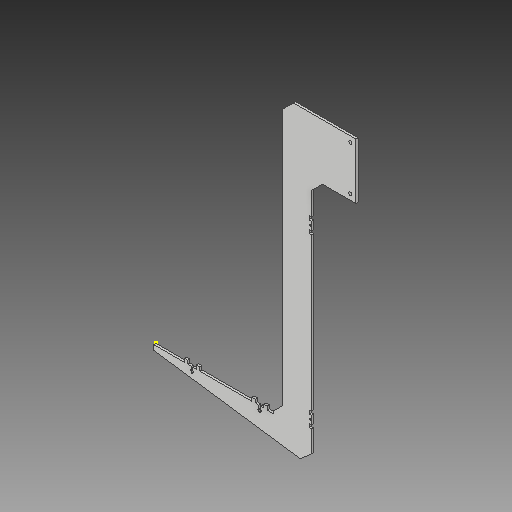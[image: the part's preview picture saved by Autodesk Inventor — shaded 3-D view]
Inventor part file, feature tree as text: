
AUTODESK INVENTOR PART (.ipt)
format: ipt  version: 2019 (Build 230136000, 136)  size: 232,960 bytes
history: native  units: in
note: dims shown in document units (in); Inventor stores cm internally (conversion verified against a paired STEP export)
features: reference x13, sketch x10, extrude x7, other x6, chamfer x2, helix x1
ambient origin geometry x8: Origin, YZ Plane, XZ Plane, XY Plane, X Axis, Y Axis, Z Axis, Center Point
bodies: Solid1 (feature_tree)
feature tree (39):
  extrude  "Extrusion1"  Depth=0.1575in
  chamfer  "Chamfer1"  Distance=0.1575in
  chamfer  "Chamfer2"  Distance=0.7874in Angle=45.0deg
  sketch  "Sketch2"  dims[d7=0.7874in d8=0.125in d9=45.0deg d10=3.1496in]
  sketch  "Sketch3"  dims[d11=3.937in d12=1.0in d13=0.0in]
  sketch  "Sketch4"  dims[d14=0.1181in d15=0.1181in]
  extrude  "Extrusion2"  Depth=3.1496in
  extrude  "Extrusion3"  Depth=3.937in TaperAngle=0.0deg
  extrude  "Extrusion4"  Depth=0.1181in
  sketch  "Sketch8"  dims[d27=0.0039in]
  extrude  "Extrusion5"  Depth=1.0in TaperAngle=0.0deg
  extrude  "Extrusion6"  Depth=1.0in TaperAngle=0.0deg
  extrude  "Extrusion7"  Depth=0.0039in
  sketch  "Sketch1"  dims[d0=15.748in d1=0.055in d2=0.1575in d3=0.0in d4=0.7874in d5=0.125in d6=45.0deg]
  reference  "Reference1"
  sketch  "Sketch5"  dims[d16=1.0in d17=0.0in d18=1.0in d19=0.0in]
  reference  "Reference2"
  reference  "Reference3"
  reference  "Reference4"
  reference  "Reference5"
  sketch  "Sketch6"  dims[d20=1.0in d21=0.0in d22=1.0in d23=0.0in]
  reference  "Reference6"
  reference  "Reference7"
  sketch  "Sketch7"  dims[d24=0.0039in d25=0.0039in d26=0.0039in]
  reference  "Reference8"
  reference  "Reference9"
  reference  "Reference10"
  sketch  "Sketch10"  dims[d28=0.2362in]
  reference  "Reference11"
  reference  "Reference12"
  sketch  "Sketch11"  dims[d29=0.2362in d30=0.3937in d31=0.3937in d32=0.3937in d33=0.3937in d34=1.0in d35=0.0in]
  reference  "Reference13"
  other  "<userpath>\Documents\CAD Files\Helix DLP\Helix DLP Z Stage.iam"
  helix  "Helix DLP Z Stage.iam"  [1 undecoded]
  other  "Print Platform:1"
  other  "Z stage_brace:1"
  other  "Maker_jigsaw_template:1"
  other  "Maker_jigsaw_template:2"
  other  "Z Stage_Linear Block Holder:1"
note: 1 required parameter value undecoded (feature->parameter linkage not recoverable at this tier; creation-order binding heuristic only, values carry confidence <= 0.55)
